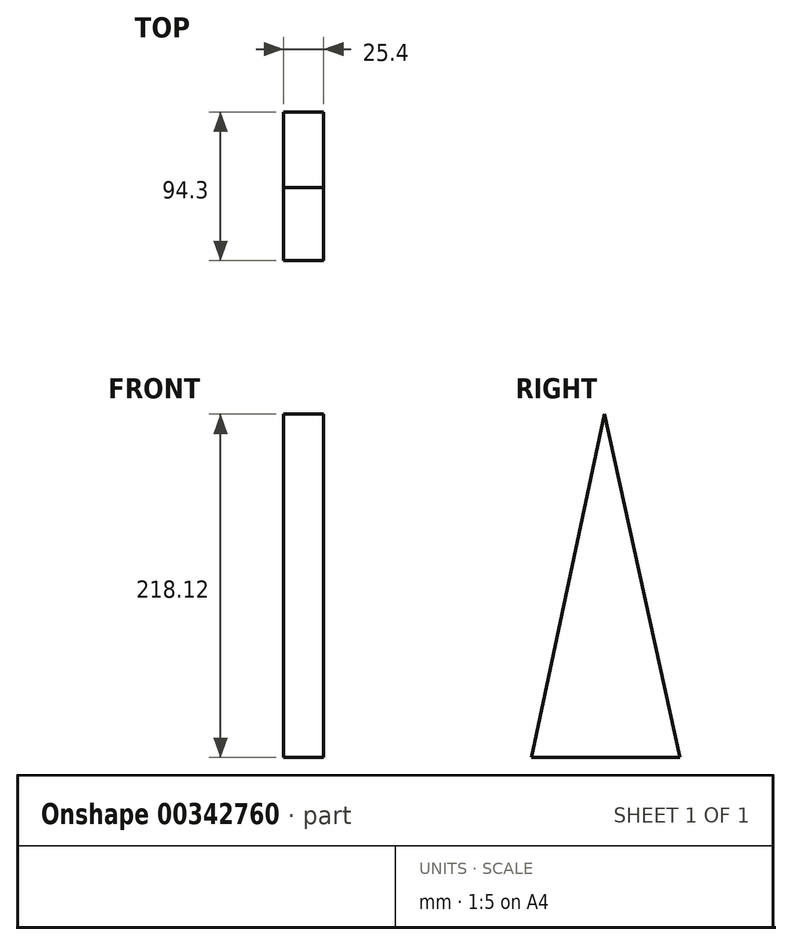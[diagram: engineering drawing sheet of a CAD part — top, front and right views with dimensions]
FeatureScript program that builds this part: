
annotation { "Feature Type Name" : "Feature", "Feature Type Description" : "" }
export const myFeature = defineFeature(function(context is Context, id is Id, definition is map)
    precondition{}
    {
        {
            var Q0;
            Q0=qCreatedBy(makeId("Right.planeOp"),FACE);
            var sketch = newSketch(context, id + "F0", { "sketchPlane" : qUnion([Q0])});
            skLineSegment(sketch, "E0", {"start": v(0, 0) * mm, "end": v(-127, 0) * mm});
            skLineSegment(sketch, "E1", {"start": v(-127, 0) * mm, "end": v(-190.5, 245.93) * mm});
            skLineSegment(sketch, "E2", {"start": v(-190.5, 245.93) * mm, "end": v(190.5, 245.93) * mm});
            skLineSegment(sketch, "E3", {"start": v(190.5, 245.93) * mm, "end": v(127, 0) * mm});
            skLineSegment(sketch, "E4", {"start": v(127, 0) * mm, "end": v(0, 0) * mm});
            skLineSegment(sketch, "E5", {"start": v(-100.65, 33.75) * mm, "end": v(-148.92, 220.7) * mm});
            skLineSegment(sketch, "E6", {"start": v(-148.92, 220.7) * mm, "end": v(-68.4, 220.7) * mm});
            skLineSegment(sketch, "E7", {"start": v(-68.4, 220.7) * mm, "end": v(-100.65, 33.75) * mm});
            skLineSegment(sketch, "E8", {"start": v(101.14, 33.14) * mm, "end": v(149.7, 221.21) * mm});
            skLineSegment(sketch, "E9", {"start": v(149.7, 221.21) * mm, "end": v(69.18, 221.21) * mm});
            skLineSegment(sketch, "E10", {"start": v(69.18, 221.21) * mm, "end": v(101.14, 33.14) * mm});
            skLineSegment(sketch, "E11", {"start": v(-46.33, 0) * mm, "end": v(0, 218.12) * mm});
            skLineSegment(sketch, "E12", {"start": v(0, 218.12) * mm, "end": v(47.97, 0) * mm});
            skLineSegment(sketch, "E13", {"start": v(47.97, 0) * mm, "end": v(-46.33, 0) * mm});
            skLineSegment(sketch, "E14", {"start": v(-7.5, 182.78) * mm, "end": v(-74.94, 182.78) * mm});
            skLineSegment(sketch, "E15", {"start": v(-74.94, 182.78) * mm, "end": v(-37.94, 39.5) * mm});
            skLineSegment(sketch, "E16", {"start": v(6.83, 187.08) * mm, "end": v(74.98, 187.08) * mm});
            skLineSegment(sketch, "E17", {"start": v(74.98, 187.08) * mm, "end": v(38.17, 44.54) * mm});
            skSolve(sketch);
        }
        {
            var Q0;
            {var subQ8=sQuery(id+"F0.wireOp",EDGE,"E0");Q0=makeQuery(id+"F0.imprint","IMPRINT",FACE,{"disambiguationData":[TD([[makeQuery(id+"F0.imprint","IMPRINT",EDGE,{"derivedFrom":subQ8}),-1.0]])]});}
            var sketch = newSketch(context, id + "F1", { "sketchPlane" : qUnion([Q0])});
            skSolve(sketch);
        }
        {
            var Q0;
            Q0 = qSketchRegion(id + "F1", true);
            var Q1;
            Q1=sQuery(id+"F0.wireOp",EDGE,"E7");
            var Q2;
            Q2=sQuery(id+"F0.wireOp",EDGE,"E6");
            var Q3;
            Q3=sQuery(id+"F0.wireOp",EDGE,"E5");
            extrude(context, id + "F2", {"entities" : qUnion([Q0]), "bodyType" : ToolBodyType.SURFACE, "surfaceEntities" : qUnion([Q1, Q2, Q3]), "depth" : 25.4 * mm});
        }
        {
            var Q0;
            {var subQ8=sQuery(id+"F0.wireOp",EDGE,"E0");Q0=makeQuery(id+"F1.imprint","IMPRINT",FACE,{"disambiguationData":[TD([[makeQuery(id+"F1.imprint","IMPRINT",EDGE,{"derivedFrom":makeQuery(id+"F0.imprint","IMPRINT",EDGE,{"derivedFrom":subQ8})}),-1.0]])]});}
            extrude(context, id + "F3", {"entities" : qUnion([Q0]), "depth" : 25.4 * mm});
        }
        {
            var Q0;
            {var subQ8=sQuery(id+"F0.wireOp",EDGE,"E0");Q0=makeQuery(id+"F1.imprint","IMPRINT",FACE,{"disambiguationData":[TD([[makeQuery(id+"F1.imprint","IMPRINT",EDGE,{"derivedFrom":makeQuery(id+"F0.imprint","IMPRINT",EDGE,{"derivedFrom":subQ8})}),-1.0]])]});}
            var Q1;
            {var subQ0=sQuery(id+"F0.wireOp",EDGE,"E8");Q1=makeQuery(id+"F1.imprint","IMPRINT",FACE,{"disambiguationData":[TD([[makeQuery(id+"F1.imprint","IMPRINT",EDGE,{"derivedFrom":makeQuery(id+"F0.imprint","IMPRINT",EDGE,{"derivedFrom":subQ0})}),1.0]])]});}
            extrude(context, id + "F4", {"entities" : qUnion([Q0, Q1]), "depth" : 25.4 * mm});
        }
    });
